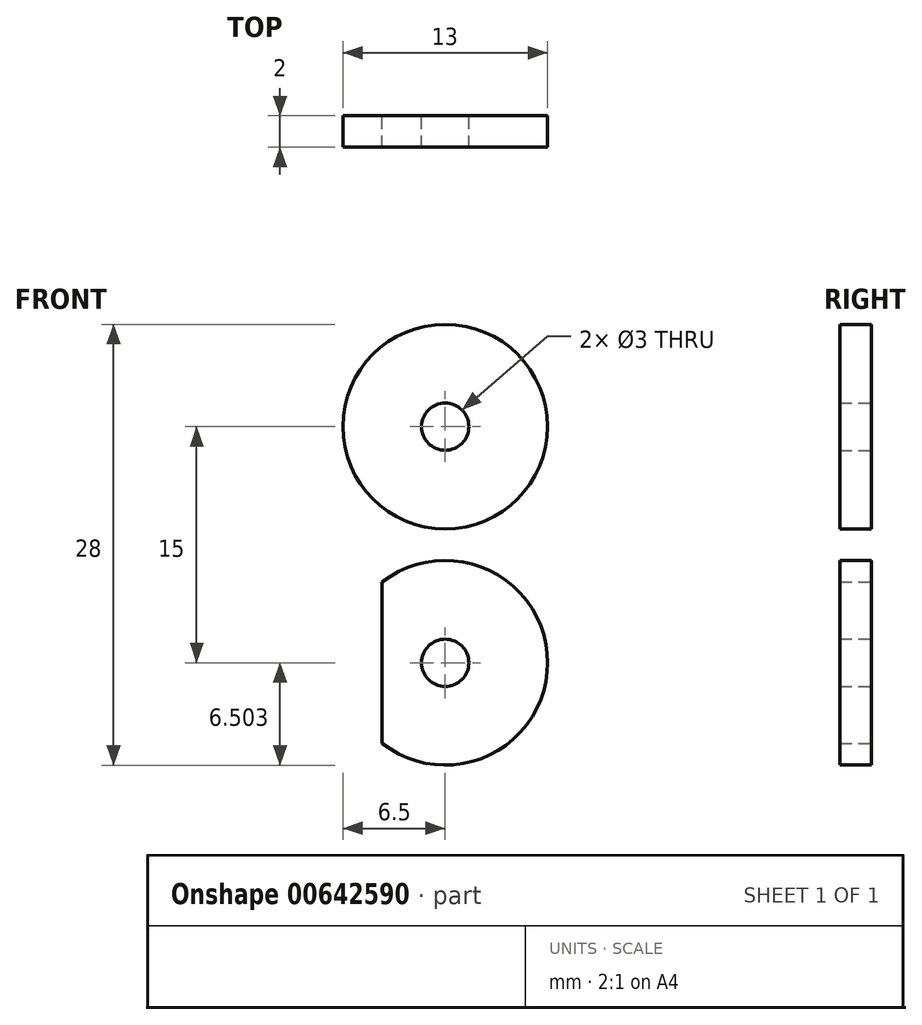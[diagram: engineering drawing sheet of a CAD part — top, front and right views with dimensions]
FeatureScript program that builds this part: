
annotation { "Feature Type Name" : "Feature", "Feature Type Description" : "" }
export const myFeature = defineFeature(function(context is Context, id is Id, definition is map)
    precondition{}
    {
        {
            var Q0;
            Q0=qCreatedBy(makeId("Front.planeOp"),FACE);
            var sketch = newSketch(context, id + "F0", { "sketchPlane" : qUnion([Q0])});
            skCircle(sketch, "E0", {"center": v(-45.97, 46.85) * mm, "radius": 1.5 * mm});
            skCircle(sketch, "E1.0", {"center": v(-45.97, 46.85) * mm, "radius": 6.5 * mm});
            skCircle(sketch, "E2", {"center": v(-45.97, 31.85) * mm, "radius": 1.5 * mm});
            skArc(sketch, "E3.0", {"start": v(-49.97, 26.73) * mm, "mid": v(-39.47, 31.85) * mm, "end": v(-49.97, 36.98) * mm});
            skLineSegment(sketch, "E4", {"start": v(-49.97, 36.98) * mm, "end": v(-49.97, 26.73) * mm});
            skSolve(sketch);
        }
        {
            var Q0;
            Q0=makeQuery(id+"F0.imprint","IMPRINT",FACE,{"disambiguationData":[TD([[makeQuery(id+"F0.imprint","IMPRINT",EDGE,{"derivedFrom":sQuery(id+"F0.wireOp",EDGE,"E0")}),-1.0]])]});
            var Q1;
            Q1=makeQuery(id+"F0.imprint","IMPRINT",FACE,{"disambiguationData":[TD([[makeQuery(id+"F0.imprint","IMPRINT",EDGE,{"derivedFrom":sQuery(id+"F0.wireOp",EDGE,"E2")}),-1.0]])]});
            extrude(context, id + "F1", {"entities" : qUnion([Q0, Q1]), "depth" : 2 * mm, "offsetDistance" : 25 * mm});
        }
    });
